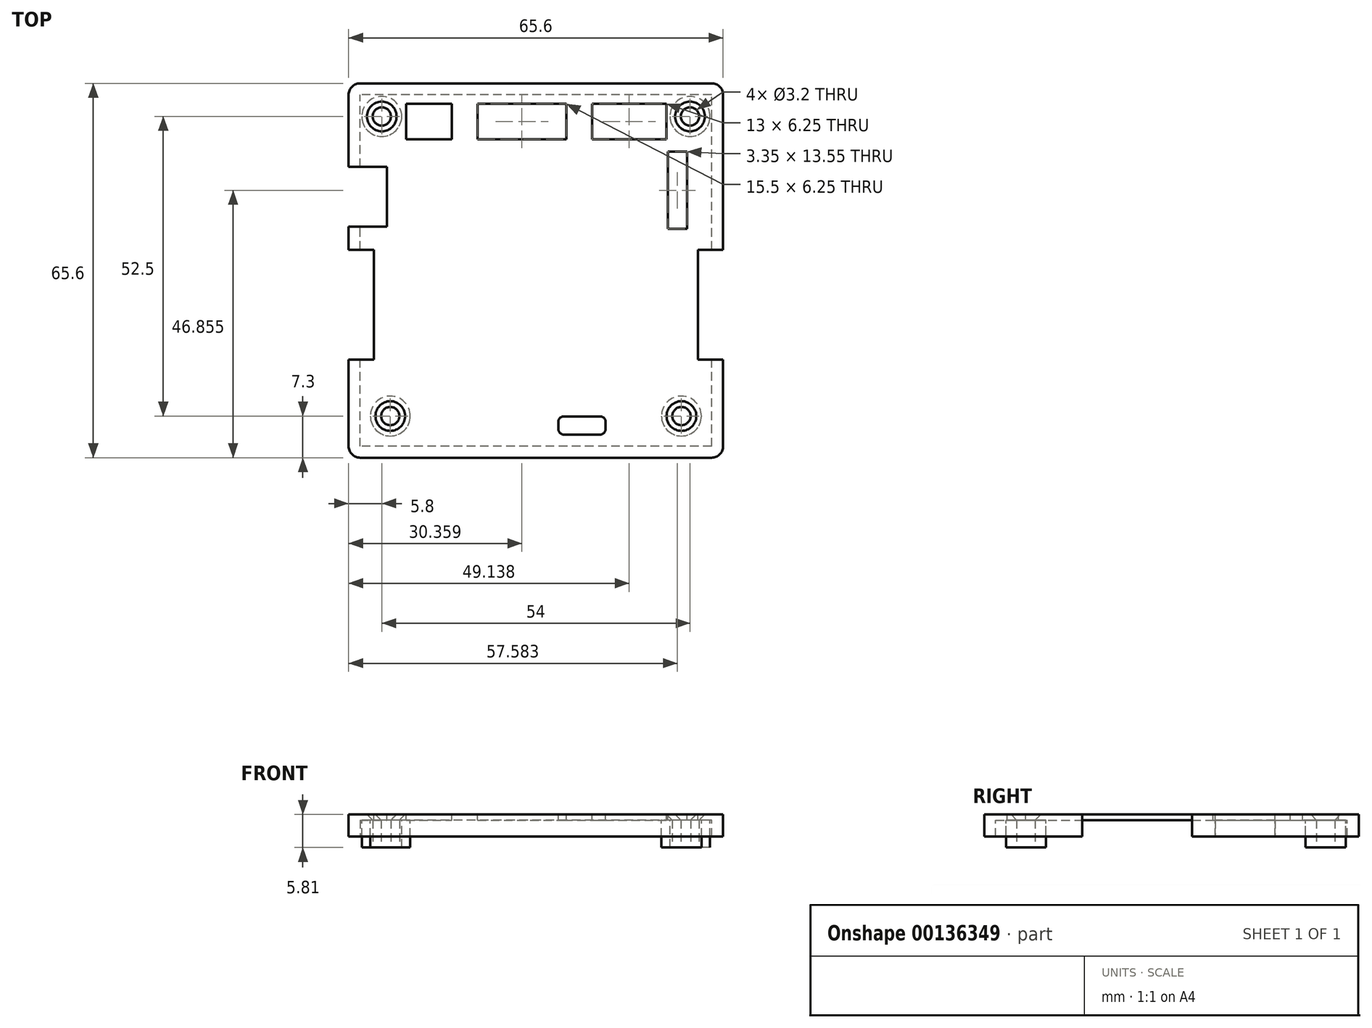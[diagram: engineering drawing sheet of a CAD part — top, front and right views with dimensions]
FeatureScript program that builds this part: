
annotation { "Feature Type Name" : "Feature", "Feature Type Description" : "" }
export const myFeature = defineFeature(function(context is Context, id is Id, definition is map)
    precondition{}
    {
        {
            var Q0;
            Q0=qCreatedBy(makeId("Top.planeOp"),FACE);
            var sketch = newSketch(context, id + "F0", { "sketchPlane" : qUnion([Q0])});
            skLineSegment(sketch, "E0.bottom", {"start": v(0, 0) * mm, "end": v(-65.6, 0) * mm});
            skLineSegment(sketch, "E0.top", {"start": v(0, 65.6) * mm, "end": v(-65.6, 65.6) * mm});
            skLineSegment(sketch, "E0.left", {"start": v(0, 0) * mm, "end": v(0, 65.6) * mm});
            skLineSegment(sketch, "E0.right", {"start": v(-65.6, 0) * mm, "end": v(-65.6, 65.6) * mm});
            skCircle(sketch, "E1", {"center": v(-59.8, 59.8) * mm, "radius": 1.6 * mm});
            skCircle(sketch, "E2", {"center": v(-5.8, 59.8) * mm, "radius": 1.6 * mm});
            skCircle(sketch, "E3", {"center": v(-58.3, 7.3) * mm, "radius": 1.6 * mm});
            skCircle(sketch, "E4", {"center": v(-7.3, 7.3) * mm, "radius": 1.6 * mm});
            skLineSegment(sketch, "E5", {"start": v(-59.8, 59.8) * mm, "end": v(-5.8, 59.8) * mm, "construction": true});
            skLineSegment(sketch, "E6.0", {"start": v(-2, 63.6) * mm, "end": v(-63.6, 63.6) * mm});
            skLineSegment(sketch, "E6.1", {"start": v(-2, 2) * mm, "end": v(-2, 63.6) * mm});
            skLineSegment(sketch, "E6.2", {"start": v(-2, 2) * mm, "end": v(-63.6, 2) * mm});
            skLineSegment(sketch, "E6.3", {"start": v(-63.6, 2) * mm, "end": v(-63.6, 63.6) * mm});
            skLineSegment(sketch, "E7", {"start": v(-58.3, 7.3) * mm, "end": v(-7.3, 7.3) * mm, "construction": true});
            skSolve(sketch);
        }
        {
            var Q0;
            Q0 = qSketchRegion(id + "F0", true);
            var Q1;
            Q1=makeQuery(id+"F0.imprint","IMPRINT",FACE,{"disambiguationData":[TD([[makeQuery(id+"F0.imprint","IMPRINT",EDGE,{"derivedFrom":sQuery(id+"F0.wireOp",EDGE,"E1")}),-1.0]])]});
            extrude(context, id + "F1", {"entities" : qUnion([Q0, Q1]), "depth" : 1 * mm});
        }
        {
            var Q0;
            Q0 = qSketchRegion(id + "F0", true);
            extrude(context, id + "F2", {"entities" : qUnion([Q0]), "operationType" : NewBodyOperationType.ADD, "oppositeDirection" : true, "depth" : 2.91 * mm});
        }
        {
            var Q0;
            Q0=makeQuery(id+"F1.opExtrude","CAP_FACE",FACE,{"disambiguationData":[OSD([sQuery(id+"F0.wireOp",EDGE,"E0.bottom"),sQuery(id+"F0.wireOp",EDGE,"E0.top"),sQuery(id+"F0.wireOp",EDGE,"E0.left"),sQuery(id+"F0.wireOp",EDGE,"E0.right"),sQuery(id+"F0.wireOp",EDGE,"E1"),sQuery(id+"F0.wireOp",EDGE,"E2"),sQuery(id+"F0.wireOp",EDGE,"E3"),sQuery(id+"F0.wireOp",EDGE,"E4")])],"isStart":false});
            var sketch = newSketch(context, id + "F3", { "sketchPlane" : qUnion([Q0])});
            skLineSegment(sketch, "E8.bottom", {"start": v(-65.6, 17.18) * mm, "end": v(-61.18, 17.18) * mm});
            skLineSegment(sketch, "E8.top", {"start": v(-65.6, 36.43) * mm, "end": v(-61.18, 36.43) * mm});
            skLineSegment(sketch, "E8.left", {"start": v(-65.6, 17.18) * mm, "end": v(-65.6, 36.43) * mm});
            skLineSegment(sketch, "E8.right", {"start": v(-61.18, 17.18) * mm, "end": v(-61.18, 36.43) * mm});
            skLineSegment(sketch, "E9.bottom", {"start": v(0, 36.43) * mm, "end": v(-4.42, 36.43) * mm});
            skLineSegment(sketch, "E9.top", {"start": v(0, 17.18) * mm, "end": v(-4.42, 17.18) * mm});
            skLineSegment(sketch, "E9.left", {"start": v(0, 36.43) * mm, "end": v(0, 17.18) * mm});
            skLineSegment(sketch, "E9.right", {"start": v(-4.42, 36.43) * mm, "end": v(-4.42, 17.18) * mm});
            skLineSegment(sketch, "E10", {"start": v(-61.18, 36.43) * mm, "end": v(-4.42, 36.43) * mm, "construction": true});
            skLineSegment(sketch, "E11", {"start": v(-61.18, 17.18) * mm, "end": v(-4.42, 17.18) * mm, "construction": true});
            skLineSegment(sketch, "E12.bottom", {"start": v(-65.6, 50.95) * mm, "end": v(-58.92, 50.95) * mm});
            skLineSegment(sketch, "E12.top", {"start": v(-65.6, 40.46) * mm, "end": v(-58.92, 40.46) * mm});
            skLineSegment(sketch, "E12.left", {"start": v(-65.6, 50.95) * mm, "end": v(-65.6, 40.46) * mm});
            skLineSegment(sketch, "E12.right", {"start": v(-58.92, 50.95) * mm, "end": v(-58.92, 40.46) * mm});
            skLineSegment(sketch, "E13.bottom", {"start": v(-55.52, 62.04) * mm, "end": v(-47.52, 62.04) * mm});
            skLineSegment(sketch, "E13.top", {"start": v(-55.52, 55.79) * mm, "end": v(-47.52, 55.79) * mm});
            skLineSegment(sketch, "E13.left", {"start": v(-55.52, 62.04) * mm, "end": v(-55.52, 55.79) * mm});
            skLineSegment(sketch, "E13.right", {"start": v(-47.52, 62.04) * mm, "end": v(-47.52, 55.79) * mm});
            skLineSegment(sketch, "E14", {"start": v(-47.52, 62.04) * mm, "end": v(-43, 62.04) * mm, "construction": true});
            skLineSegment(sketch, "E15.bottom", {"start": v(-43, 62.04) * mm, "end": v(-27.5, 62.04) * mm});
            skLineSegment(sketch, "E15.top", {"start": v(-43, 55.79) * mm, "end": v(-27.5, 55.79) * mm});
            skLineSegment(sketch, "E15.left", {"start": v(-43, 62.04) * mm, "end": v(-43, 55.79) * mm});
            skLineSegment(sketch, "E15.right", {"start": v(-27.5, 62.04) * mm, "end": v(-27.5, 55.79) * mm});
            skLineSegment(sketch, "E16", {"start": v(-47.52, 55.79) * mm, "end": v(-43, 55.79) * mm, "construction": true});
            skLineSegment(sketch, "E17", {"start": v(-27.5, 62.04) * mm, "end": v(-22.96, 62.04) * mm, "construction": true});
            skLineSegment(sketch, "E18.bottom", {"start": v(-22.96, 62.04) * mm, "end": v(-9.96, 62.04) * mm});
            skLineSegment(sketch, "E18.top", {"start": v(-22.96, 55.79) * mm, "end": v(-9.96, 55.79) * mm});
            skLineSegment(sketch, "E18.left", {"start": v(-22.96, 62.04) * mm, "end": v(-22.96, 55.79) * mm});
            skLineSegment(sketch, "E18.right", {"start": v(-9.96, 62.04) * mm, "end": v(-9.96, 55.79) * mm});
            skLineSegment(sketch, "E19", {"start": v(-22.96, 55.79) * mm, "end": v(-27.5, 55.79) * mm, "construction": true});
            skLineSegment(sketch, "E20.bottom", {"start": v(-28.88, 7.24) * mm, "end": v(-20.58, 7.24) * mm});
            skLineSegment(sketch, "E20.top", {"start": v(-28.88, 4.04) * mm, "end": v(-20.58, 4.04) * mm});
            skLineSegment(sketch, "E20.left", {"start": v(-28.88, 7.24) * mm, "end": v(-28.88, 4.04) * mm});
            skLineSegment(sketch, "E20.right", {"start": v(-20.58, 7.24) * mm, "end": v(-20.58, 4.04) * mm});
            skLineSegment(sketch, "E21.bottom", {"start": v(-6.34, 40.08) * mm, "end": v(-9.7, 40.08) * mm});
            skLineSegment(sketch, "E21.top", {"start": v(-6.34, 53.63) * mm, "end": v(-9.7, 53.63) * mm});
            skLineSegment(sketch, "E21.left", {"start": v(-6.34, 40.08) * mm, "end": v(-6.34, 53.63) * mm});
            skLineSegment(sketch, "E21.right", {"start": v(-9.7, 40.08) * mm, "end": v(-9.7, 53.63) * mm});
            skSolve(sketch);
        }
        {
            var Q0;
            Q0=makeQuery(id+"F3.imprint","IMPRINT",FACE,{"disambiguationData":[TD([[makeQuery(id+"F3.imprint","IMPRINT",EDGE,{"derivedFrom":sQuery(id+"F3.wireOp",EDGE,"E8.bottom")}),1.0]])]});
            var Q1;
            Q1=makeQuery(id+"F3.imprint","IMPRINT",FACE,{"disambiguationData":[TD([[makeQuery(id+"F3.imprint","IMPRINT",EDGE,{"derivedFrom":sQuery(id+"F3.wireOp",EDGE,"E9.bottom")}),1.0]])]});
            var Q2;
            Q2=makeQuery(id+"F3.imprint","IMPRINT",FACE,{"disambiguationData":[TD([[makeQuery(id+"F3.imprint","IMPRINT",EDGE,{"derivedFrom":sQuery(id+"F3.wireOp",EDGE,"E12.bottom")}),-1.0]])]});
            var Q3;
            Q3=makeQuery(id+"F3.imprint","IMPRINT",FACE,{"disambiguationData":[TD([[makeQuery(id+"F3.imprint","IMPRINT",EDGE,{"derivedFrom":sQuery(id+"F3.wireOp",EDGE,"E13.bottom")}),-1.0]])]});
            var Q4;
            Q4=makeQuery(id+"F3.imprint","IMPRINT",FACE,{"disambiguationData":[TD([[makeQuery(id+"F3.imprint","IMPRINT",EDGE,{"derivedFrom":sQuery(id+"F3.wireOp",EDGE,"E15.bottom")}),-1.0]])]});
            var Q5;
            Q5=makeQuery(id+"F3.imprint","IMPRINT",FACE,{"disambiguationData":[TD([[makeQuery(id+"F3.imprint","IMPRINT",EDGE,{"derivedFrom":sQuery(id+"F3.wireOp",EDGE,"E18.bottom")}),-1.0]])]});
            var Q6;
            Q6=makeQuery(id+"F3.imprint","IMPRINT",FACE,{"disambiguationData":[TD([[makeQuery(id+"F3.imprint","IMPRINT",EDGE,{"derivedFrom":sQuery(id+"F3.wireOp",EDGE,"E20.bottom")}),-1.0]])]});
            var Q7;
            Q7=makeQuery(id+"F3.imprint","IMPRINT",FACE,{"disambiguationData":[TD([[makeQuery(id+"F3.imprint","IMPRINT",EDGE,{"derivedFrom":sQuery(id+"F3.wireOp",EDGE,"E21.bottom")}),-1.0]])]});
            extrude(context, id + "F4", {"entities" : qUnion([Q0, Q1, Q2, Q3, Q4, Q5, Q6, Q7]), "operationType" : NewBodyOperationType.REMOVE, "endBound" : BoundingType.THROUGH_ALL, "oppositeDirection" : true, "depth" : 25 * mm});
        }
        {
            var Q0;
            Q0=makeQuery(id+"F4.boolean.opBoolean","COPY",EDGE,{"derivedFrom":makeQuery(id+"F4.opExtrude","SWEPT_EDGE",EDGE,{"disambiguationData":[OSD([sQuery(id+"F3.wireOp",EDGE,"E20.bottom"),sQuery(id+"F3.wireOp",EDGE,"E20.left")])]})});
            var Q1;
            Q1=makeQuery(id+"F4.boolean.opBoolean","COPY",EDGE,{"derivedFrom":makeQuery(id+"F4.opExtrude","SWEPT_EDGE",EDGE,{"disambiguationData":[OSD([sQuery(id+"F3.wireOp",EDGE,"E20.top"),sQuery(id+"F3.wireOp",EDGE,"E20.right")])]})});
            var Q2;
            Q2=makeQuery(id+"F4.boolean.opBoolean","COPY",EDGE,{"derivedFrom":makeQuery(id+"F4.opExtrude","SWEPT_EDGE",EDGE,{"disambiguationData":[OSD([sQuery(id+"F3.wireOp",EDGE,"E20.bottom"),sQuery(id+"F3.wireOp",EDGE,"E20.right")])]})});
            var Q3;
            Q3=makeQuery(id+"F4.boolean.opBoolean","COPY",EDGE,{"derivedFrom":makeQuery(id+"F4.opExtrude","SWEPT_EDGE",EDGE,{"disambiguationData":[OSD([sQuery(id+"F3.wireOp",EDGE,"E20.top"),sQuery(id+"F3.wireOp",EDGE,"E20.left")])]})});
            fillet(context, id + "F5", {"entities" : qUnion([Q0, Q1, Q2, Q3]), "radius" : 1 * mm, "tangentPropagation" : true, "allowEdgeOverflow" : false});
        }
        {
            var Q0;
            {var subQ0=sQuery(id+"F0.wireOp",EDGE,"E0.right");var subQ1=sQuery(id+"F0.wireOp",EDGE,"E0.bottom");Q0=makeQuery(id+"F2.boolean.opBoolean","MERGE",EDGE,{"derivedFrom":[makeQuery(id+"F1.opExtrude","SWEPT_EDGE",EDGE,{"disambiguationData":[OSD([subQ1,subQ0])]}),makeQuery(id+"F2.opExtrude","SWEPT_EDGE",EDGE,{"disambiguationData":[OSD([subQ1,subQ0])]})]});}
            var Q1;
            {var subQ0=sQuery(id+"F0.wireOp",EDGE,"E0.left");var subQ1=sQuery(id+"F0.wireOp",EDGE,"E0.bottom");Q1=makeQuery(id+"F2.boolean.opBoolean","MERGE",EDGE,{"derivedFrom":[makeQuery(id+"F1.opExtrude","SWEPT_EDGE",EDGE,{"disambiguationData":[OSD([subQ1,subQ0])]}),makeQuery(id+"F2.opExtrude","SWEPT_EDGE",EDGE,{"disambiguationData":[OSD([subQ1,subQ0])]})]});}
            var Q2;
            {var subQ0=sQuery(id+"F0.wireOp",EDGE,"E0.left");var subQ1=sQuery(id+"F0.wireOp",EDGE,"E0.top");Q2=makeQuery(id+"F2.boolean.opBoolean","MERGE",EDGE,{"derivedFrom":[makeQuery(id+"F1.opExtrude","SWEPT_EDGE",EDGE,{"disambiguationData":[OSD([subQ1,subQ0])]}),makeQuery(id+"F2.opExtrude","SWEPT_EDGE",EDGE,{"disambiguationData":[OSD([subQ1,subQ0])]})]});}
            var Q3;
            {var subQ0=sQuery(id+"F0.wireOp",EDGE,"E0.right");var subQ1=sQuery(id+"F0.wireOp",EDGE,"E0.top");Q3=makeQuery(id+"F2.boolean.opBoolean","MERGE",EDGE,{"derivedFrom":[makeQuery(id+"F1.opExtrude","SWEPT_EDGE",EDGE,{"disambiguationData":[OSD([subQ1,subQ0])]}),makeQuery(id+"F2.opExtrude","SWEPT_EDGE",EDGE,{"disambiguationData":[OSD([subQ1,subQ0])]})]});}
            fillet(context, id + "F6", {"entities" : qUnion([Q0, Q1, Q2, Q3]), "radius" : 2 * mm, "tangentPropagation" : true, "allowEdgeOverflow" : false});
        }
        {
            var Q0;
            Q0=makeQuery(id+"F1.opExtrude","CAP_FACE",FACE,{"disambiguationData":[OSD([sQuery(id+"F0.wireOp",EDGE,"E0.bottom"),sQuery(id+"F0.wireOp",EDGE,"E0.top"),sQuery(id+"F0.wireOp",EDGE,"E0.left"),sQuery(id+"F0.wireOp",EDGE,"E0.right"),sQuery(id+"F0.wireOp",EDGE,"E1"),sQuery(id+"F0.wireOp",EDGE,"E2"),sQuery(id+"F0.wireOp",EDGE,"E3"),sQuery(id+"F0.wireOp",EDGE,"E4")])],"isStart":true});
            var sketch = newSketch(context, id + "F7", { "sketchPlane" : qUnion([Q0])});
            skCircle(sketch, "E22", {"center": v(-7.3, -7.3) * mm, "radius": 3.5 * mm});
            skCircle(sketch, "E23", {"center": v(-5.8, -59.8) * mm, "radius": 3.5 * mm});
            skCircle(sketch, "E24", {"center": v(-59.8, -59.8) * mm, "radius": 3.5 * mm});
            skCircle(sketch, "E25", {"center": v(-58.3, -7.3) * mm, "radius": 3.5 * mm});
            skCircle(sketch, "E26", {"center": v(-58.3, -7.3) * mm, "radius": 1.6 * mm});
            skCircle(sketch, "E27", {"center": v(-7.3, -7.3) * mm, "radius": 1.6 * mm});
            skCircle(sketch, "E28", {"center": v(-5.8, -59.8) * mm, "radius": 1.6 * mm});
            skCircle(sketch, "E29", {"center": v(-59.8, -59.8) * mm, "radius": 1.6 * mm});
            skSolve(sketch);
        }
        {
            var Q0;
            Q0 = qSketchRegion(id + "F7", true);
            extrude(context, id + "F8", {"entities" : qUnion([Q0]), "operationType" : NewBodyOperationType.ADD, "depth" : 4.8 * mm});
        }
        {
            var Q0;
            Q0=makeQuery(id+"F1.opExtrude","CAP_EDGE",EDGE,{"disambiguationData":[OSD([sQuery(id+"F0.wireOp",EDGE,"E2")])],"isStart":false});
            var Q1;
            Q1=makeQuery(id+"F1.opExtrude","CAP_EDGE",EDGE,{"disambiguationData":[OSD([sQuery(id+"F0.wireOp",EDGE,"E4")])],"isStart":false});
            var Q2;
            Q2=makeQuery(id+"F1.opExtrude","CAP_EDGE",EDGE,{"disambiguationData":[OSD([sQuery(id+"F0.wireOp",EDGE,"E3")])],"isStart":false});
            var Q3;
            Q3=makeQuery(id+"F1.opExtrude","CAP_EDGE",EDGE,{"disambiguationData":[OSD([sQuery(id+"F0.wireOp",EDGE,"E1")])],"isStart":false});
            chamfer(context, id + "F9", {"entities" : qUnion([Q0, Q1, Q2, Q3]), "width" : 1 * mm, "tangentPropagation" : true});
        }
    });
